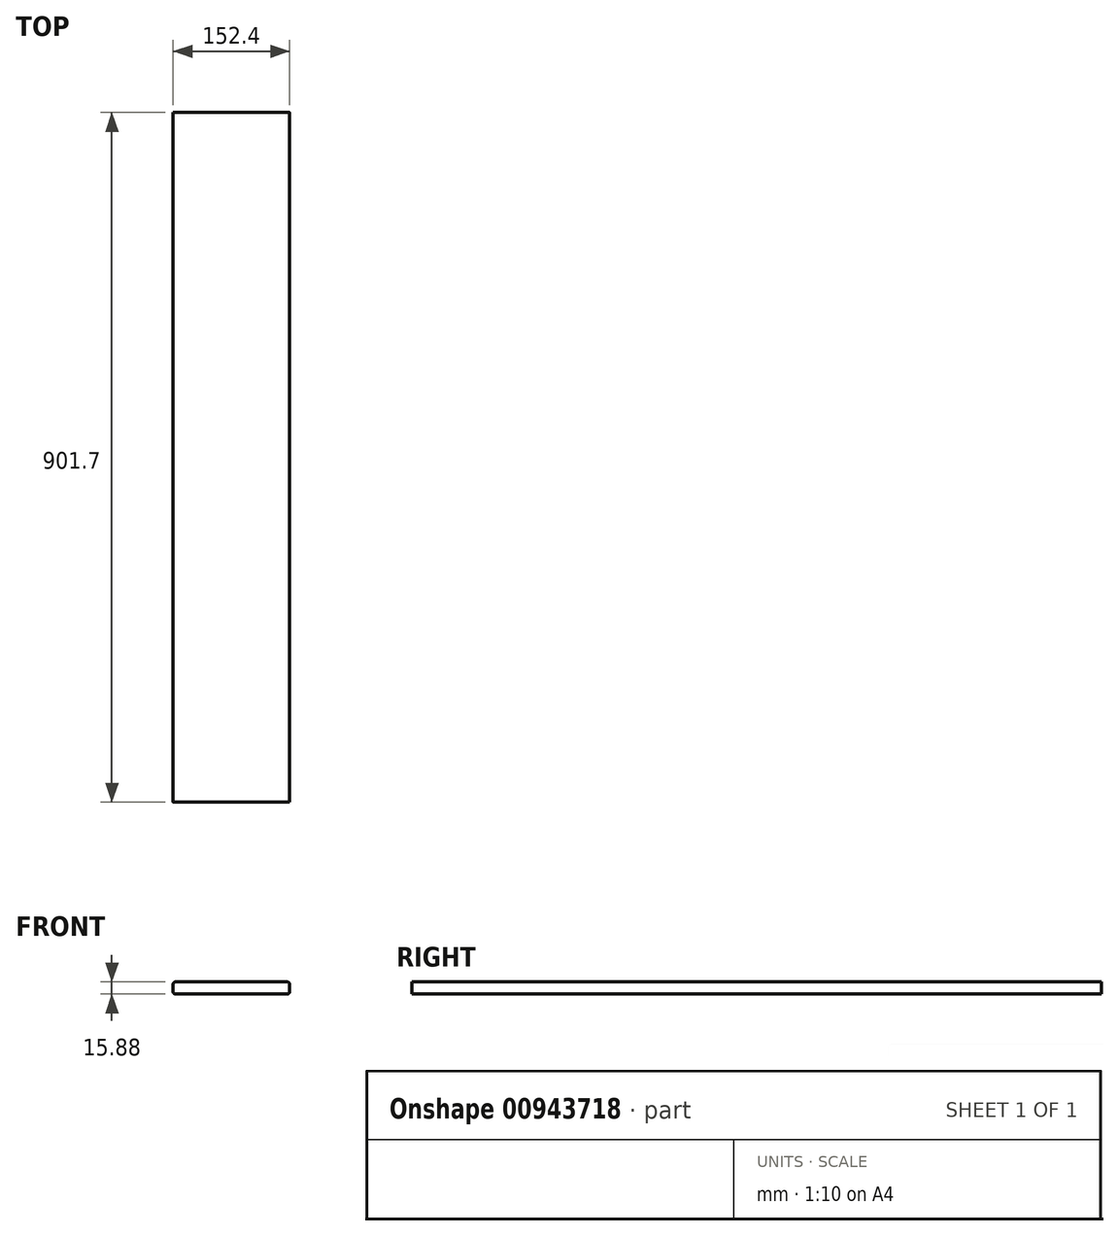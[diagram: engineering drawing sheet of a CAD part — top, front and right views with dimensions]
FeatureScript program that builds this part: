
annotation { "Feature Type Name" : "Feature", "Feature Type Description" : "" }
export const myFeature = defineFeature(function(context is Context, id is Id, definition is map)
    precondition{}
    {
        {
            var Q0;
            Q0=qCreatedBy(makeId("Front.planeOp"),FACE);
            var sketch = newSketch(context, id + "F0", { "sketchPlane" : qUnion([Q0])});
            skLineSegment(sketch, "E0.bottom", {"start": v(73.03, -7.94) * mm, "end": v(-73.03, -7.94) * mm});
            skLineSegment(sketch, "E0.top", {"start": v(73.03, 7.94) * mm, "end": v(-73.03, 7.94) * mm});
            skLineSegment(sketch, "E0.left", {"start": v(76.2, -4.76) * mm, "end": v(76.2, 4.76) * mm});
            skLineSegment(sketch, "E0.right", {"start": v(-76.2, -4.76) * mm, "end": v(-76.2, 4.76) * mm});
            skPoint(sketch, "E0.middle", {"position": v(0, 0) * mm});
            skPoint(sketch, "E1.visualSharp", {"position": v(-76.2, 7.94) * mm});
            skArc(sketch, "E1.filletArc", {"start": v(-73.03, 7.94) * mm, "mid": v(-75.27, 7) * mm, "end": v(-76.2, 4.76) * mm});
            skPoint(sketch, "E2.visualSharp", {"position": v(-76.2, -7.94) * mm});
            skArc(sketch, "E2.filletArc", {"start": v(-76.2, -4.76) * mm, "mid": v(-75.27, -7) * mm, "end": v(-73.03, -7.94) * mm});
            skPoint(sketch, "E3.visualSharp", {"position": v(76.2, 7.94) * mm});
            skArc(sketch, "E3.filletArc", {"start": v(76.2, 4.76) * mm, "mid": v(75.27, 7) * mm, "end": v(73.03, 7.94) * mm});
            skPoint(sketch, "E4.visualSharp", {"position": v(76.2, -7.94) * mm});
            skArc(sketch, "E4.filletArc", {"start": v(73.03, -7.94) * mm, "mid": v(75.27, -7) * mm, "end": v(76.2, -4.76) * mm});
            skSolve(sketch);
        }
        {
            var Q0;
            Q0=makeQuery(id+"F0.imprint","IMPRINT",FACE,{"disambiguationData":[TD([[makeQuery(id+"F0.imprint","IMPRINT",EDGE,{"derivedFrom":sQuery(id+"F0.wireOp",EDGE,"E0.bottom")}),-1.0]])]});
            extrude(context, id + "F1", {"entities" : qUnion([Q0]), "depth" : 901.7 * mm, "offsetDistance" : 25.4 * mm});
        }
    });
